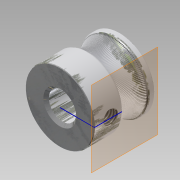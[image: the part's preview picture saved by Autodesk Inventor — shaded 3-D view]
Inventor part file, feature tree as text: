
AUTODESK INVENTOR PART (.ipt)
format: ipt  version: 2014 SP1 (Build 180222100, 222)  size: 3,423,744 bytes
history: native  units: mm
features: sketch x5, other x3, chamfer x3, hole x2, revolve x1, pattern_circular x1
ambient origin geometry x8: Origin, YZ Plane, XZ Plane, XY Plane, X Axis, Y Axis, Z Axis, Center Point
bodies: Body1 (feature_tree)
feature tree (15):
  other  "Bryła1"
  revolve  "Obrót1"
  chamfer  "Faza1"  Distance=6.3mm
  hole  "Otwór1"  [1 undecoded]
  chamfer  "Faza2"  Distance=5.0mm
  sketch  "Szkic4"
  other  "Płaszczyzna konstrukcyjna1"
  hole  "Otwór2"  [1 undecoded]
  chamfer  "Faza3"  Distance=5.3mm
  other  "Wypukłość2"
  pattern_circular  "Szyk kołowy3"  [2 undecoded]
  sketch  "Szkic1"
  sketch  "Szkic3"
  sketch  "Szkic5"
  sketch  "Szkic7"
note: 4 required parameter values undecoded (feature->parameter linkage not recoverable at this tier; creation-order binding heuristic only, values carry confidence <= 0.55)
